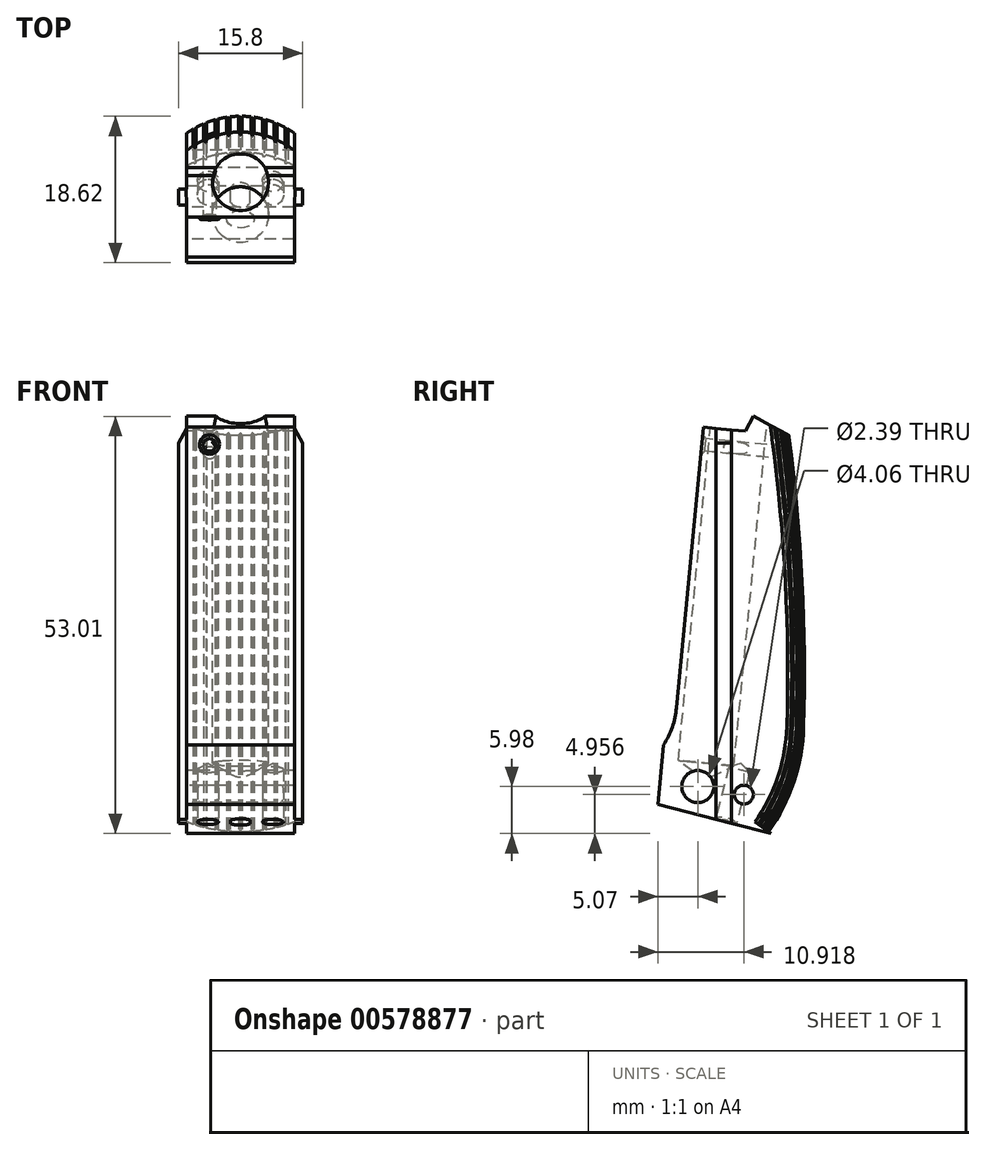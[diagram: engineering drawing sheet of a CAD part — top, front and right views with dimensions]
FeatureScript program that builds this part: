
annotation { "Feature Type Name" : "Feature", "Feature Type Description" : "" }
export const myFeature = defineFeature(function(context is Context, id is Id, definition is map)
    precondition{}
    {
        {
            var Q0;
            Q0=qCreatedBy(makeId("Right.planeOp"),FACE);
            var sketch = newSketch(context, id + "F0", { "sketchPlane" : qUnion([Q0])});
            skCircle(sketch, "E0", {"center": v(0, 0) * mm, "radius": 2.03 * mm});
            skLineSegment(sketch, "E1", {"start": v(-2.71, 10) * mm, "end": v(0.72, 45.66) * mm});
            skLineSegment(sketch, "E2", {"start": v(-5.07, -2.27) * mm, "end": v(-4.34, 5.28) * mm});
            skArc(sketch, "E3", {"start": v(-2.71, 10) * mm, "mid": v(-3.25, 7.55) * mm, "end": v(-4.34, 5.28) * mm});
            skLineSegment(sketch, "E4", {"start": v(-12.8, 17) * mm, "end": v(-15.23, -8.22) * mm, "construction": true});
            skLineSegment(sketch, "E5", {"start": v(0.72, 45.66) * mm, "end": v(6.03, 45.15) * mm});
            skLineSegment(sketch, "E6", {"start": v(-15.2, 11.21) * mm, "end": v(-11.58, 10.86) * mm, "construction": true});
            skLineSegment(sketch, "E7", {"start": v(-5.07, -2.27) * mm, "end": v(9.27, -5.98) * mm});
            skLineSegment(sketch, "E8", {"start": v(6.03, 45.15) * mm, "end": v(7.03, 47.03) * mm});
            skLineSegment(sketch, "E9", {"start": v(7.03, 47.03) * mm, "end": v(11.94, 44.43) * mm});
            skLineSegment(sketch, "E10", {"start": v(0.37, 1.43) * mm, "end": v(-0.87, -3.35) * mm, "construction": true});
            skLineSegment(sketch, "E11", {"start": v(5.64, -1.84) * mm, "end": v(6.05, -0.23) * mm, "construction": true});
            skLineSegment(sketch, "E12", {"start": v(-1.42, 0.37) * mm, "end": v(1.46, -0.38) * mm, "construction": true});
            skLineSegment(sketch, "E13", {"start": v(5.18, -0.85) * mm, "end": v(6.43, -1.18) * mm, "construction": true});
            skPoint(sketch, "E14", {"position": v(5.85, -1.02) * mm});
            skCircle(sketch, "E15", {"center": v(5.85, -1.02) * mm, "radius": 1.2 * mm});
            skLineSegment(sketch, "E16", {"start": v(-2.99, 1.59) * mm, "end": v(23.37, -12.43) * mm, "construction": true});
            skArc(sketch, "E17", {"start": v(13.82, 7.56) * mm, "mid": v(12.55, 0.45) * mm, "end": v(9.27, -5.98) * mm});
            skLineSegment(sketch, "E18", {"start": v(-9.64, 20.45) * mm, "end": v(-11.98, -3.86) * mm, "construction": true});
            skArc(sketch, "E19", {"start": v(10.4, 54.37) * mm, "mid": v(11.22, 49.4) * mm, "end": v(11.94, 44.43) * mm, "construction": true});
            skLineSegment(sketch, "E20", {"start": v(4.58, 39.64) * mm, "end": v(6.07, 55.07) * mm, "construction": true});
            skLineSegment(sketch, "E21", {"start": v(1.76, 47.46) * mm, "end": v(1, 39.47) * mm, "construction": true});
            skLineSegment(sketch, "E22", {"start": v(8.96, 48.04) * mm, "end": v(8.09, 38.96) * mm, "construction": true});
            skPoint(sketch, "E23", {"position": v(8.78, 46.1) * mm});
            skPoint(sketch, "E24", {"position": v(8, -5.64) * mm});
            skLineSegment(sketch, "E25", {"start": v(0, 44.43) * mm, "end": v(17.1, 44.43) * mm, "construction": true});
            skPoint(sketch, "E26", {"position": v(11.94, 44.43) * mm});
            skPoint(sketch, "E27.orphan", {"position": v(10.52, 45.18) * mm});
            skArc(sketch, "E28", {"start": v(10.41, -4.22) * mm, "mid": v(8.76, -6.67) * mm, "end": v(6.82, -8.91) * mm, "construction": true});
            skArc(sketch, "E29", {"start": v(11.94, 44.43) * mm, "mid": v(13.62, 26.03) * mm, "end": v(13.82, 7.56) * mm});
            skPoint(sketch, "E30", {"position": v(-2.83, -2.85) * mm});
            skSolve(sketch);
        }
        {
            var Q0;
            Q0=makeQuery(id+"F0.imprint","IMPRINT",FACE,{"disambiguationData":[TD([[makeQuery(id+"F0.imprint","IMPRINT",EDGE,{"derivedFrom":sQuery(id+"F0.wireOp",EDGE,"E0")}),-1.0]])]});
            extrude(context, id + "F1", {"entities" : qUnion([Q0]), "endBound" : BoundingType.SYMMETRIC, "depth" : 13.67 * mm});
        }
        {
            var Q0;
            Q0=makeQuery(id+"F1.opExtrude","CAP_FACE",FACE,{"disambiguationData":[OSD([sQuery(id+"F0.wireOp",EDGE,"E0"),sQuery(id+"F0.wireOp",EDGE,"E1"),sQuery(id+"F0.wireOp",EDGE,"E2"),sQuery(id+"F0.wireOp",EDGE,"E3"),sQuery(id+"F0.wireOp",EDGE,"E5"),sQuery(id+"F0.wireOp",EDGE,"E7"),sQuery(id+"F0.wireOp",EDGE,"E8"),sQuery(id+"F0.wireOp",EDGE,"E9"),sQuery(id+"F0.wireOp",EDGE,"E15"),sQuery(id+"F0.wireOp",EDGE,"E17"),sQuery(id+"F0.wireOp",EDGE,"E19"),sQuery(id+"F0.wireOp",EDGE,"37774267-7ef6-4adb-93f1-0c025de73d9b")])],"isStart":false});
            var sketch = newSketch(context, id + "F2", { "sketchPlane" : qUnion([Q0])});
            skLineSegment(sketch, "E31", {"start": v(2.29, 45.5) * mm, "end": v(2.29, -4.17) * mm});
            skLineSegment(sketch, "E32", {"start": v(4.27, 45.32) * mm, "end": v(4.27, -4.68) * mm});
            skLineSegment(sketch, "E33.0", {"start": v(2.29, 45.5) * mm, "end": v(4.27, 45.32) * mm});
            skPoint(sketch, "E34.orphan", {"position": v(0.72, 45.66) * mm});
            skPoint(sketch, "E35.orphan", {"position": v(6.03, 45.15) * mm});
            skLineSegment(sketch, "E36.0", {"start": v(2.29, -4.17) * mm, "end": v(4.27, -4.68) * mm});
            skPoint(sketch, "E37.orphan", {"position": v(-5.07, -2.27) * mm});
            skSolve(sketch);
        }
        {
            var Q0;
            Q0=makeQuery(id+"F2.imprint","IMPRINT",FACE,{"disambiguationData":[TD([[makeQuery(id+"F2.imprint","IMPRINT",EDGE,{"derivedFrom":sQuery(id+"F2.wireOp",EDGE,"E31")}),1.0]])]});
            var Q1;
            Q1=qSketchRegion(id+"F2",true);
            extrude(context, id + "F3", {"entities" : qUnion([Q0, Q1]), "operationType" : NewBodyOperationType.ADD, "depth" : 1.07 * mm});
        }
        {
            var Q0;
            {var subQ0=makeQuery(id+"F3.boolean.opBoolean","MERGE",FACE,{"derivedFrom":[makeQuery(id+"F1.opExtrude","SWEPT_FACE",FACE,{"disambiguationData":[OSD([sQuery(id+"F0.wireOp",EDGE,"E5")])]}),makeQuery(id+"F3.opExtrude","SWEPT_FACE",FACE,{"disambiguationData":[OSD([sQuery(id+"F2.wireOp",EDGE,"E33.0")])]})]});Q0=makeQuery(id+"F10.boolean.opBoolean","MERGE",FACE,{"derivedFrom":[subQ0,makeQuery(id+"F10.opPattern","COPY",FACE,{"derivedFrom":subQ0,"instanceName":"1"})]});}
            var sketch = newSketch(context, id + "F4", { "sketchPlane" : qUnion([Q0])});
            skCircle(sketch, "E38", {"center": v(0, 0.76) * mm, "radius": 3.56 * mm});
            skSolve(sketch);
        }
        {
            var Q0;
            Q0=qSketchRegion(id+"F4",true);
            extrude(context, id + "F5", {"entities" : qUnion([Q0]), "operationType" : NewBodyOperationType.REMOVE, "oppositeDirection" : true, "depth" : 42.47 * mm, "hasSecondDirection" : true, "secondDirectionOppositeDirection" : false, "secondDirectionDepth" : 25.4 * mm});
        }
        {
            var Q0;
            Q0=makeQuery(id+"F3.opExtrude","SWEPT_FACE",FACE,{"disambiguationData":[OSD([sQuery(id+"F2.wireOp",EDGE,"E31")])]});
            var sketch = newSketch(context, id + "F6", { "sketchPlane" : qUnion([Q0])});
            skLineSegment(sketch, "E39.0", {"start": v(7.9, 45.5) * mm, "end": v(6.83, 45.5) * mm});
            skLineSegment(sketch, "E40.0", {"start": v(7.9, 45.5) * mm, "end": v(7.9, 43.66) * mm});
            skLineSegment(sketch, "E41", {"start": v(6.83, 45.5) * mm, "end": v(7.9, 43.66) * mm});
            skPoint(sketch, "E42.0.end.orphan", {"position": v(6.83, -4.68) * mm});
            skPoint(sketch, "E43.orphan", {"position": v(7.9, -4.17) * mm});
            skSolve(sketch);
        }
        {
            var Q0;
            Q0=makeQuery(id+"F6.imprint","IMPRINT",FACE,{"disambiguationData":[TD([[makeQuery(id+"F6.imprint","IMPRINT",EDGE,{"derivedFrom":sQuery(id+"F6.wireOp",EDGE,"E39.0")}),1.0]])]});
            extrude(context, id + "F7", {"entities" : qUnion([Q0]), "operationType" : NewBodyOperationType.REMOVE, "endBound" : BoundingType.THROUGH_ALL, "oppositeDirection" : true, "depth" : 25.4 * mm});
        }
        {
            var Q0;
            Q0=qCreatedBy(makeId("Right.planeOp"),FACE);
            var sketch = newSketch(context, id + "F8", { "sketchPlane" : qUnion([Q0])});
            skLineSegment(sketch, "E44.0", {"start": v(-2.49, 3.3) * mm, "end": v(1.05, 2.96) * mm});
            skPoint(sketch, "E45", {"position": v(1.05, 2.96) * mm});
            skLineSegment(sketch, "E46", {"start": v(1.05, 2.96) * mm, "end": v(0.85, 0.83) * mm});
            skLineSegment(sketch, "E47", {"start": v(0.85, 0.83) * mm, "end": v(-2.49, 3.3) * mm});
            skPoint(sketch, "E48.orphan", {"position": v(4.6, 2.62) * mm});
            skSolve(sketch);
        }
        {
            var Q0;
            Q0=qSketchRegion(id+"F8",true);
            var Q1;
            Q1=sQuery(id+"F8.wireOp",EDGE,"E46");
            revolve(context, id + "F9", {"operationType" : NewBodyOperationType.REMOVE, "entities" : qUnion([Q0]), "axis" : qUnion([Q1]), "revolveType" : RevolveType.FULL, "oppositeDirection" : true});
        }
        {
            var Q0;
            Q0=makeQuery(id+"F1.opExtrude","SWEPT_BODY",BODY,{"disambiguationData":[OSD([sQuery(id+"F0.wireOp",EDGE,"E0"),sQuery(id+"F0.wireOp",EDGE,"E1"),sQuery(id+"F0.wireOp",EDGE,"E2"),sQuery(id+"F0.wireOp",EDGE,"E3"),sQuery(id+"F0.wireOp",EDGE,"E5"),sQuery(id+"F0.wireOp",EDGE,"E7"),sQuery(id+"F0.wireOp",EDGE,"E8"),sQuery(id+"F0.wireOp",EDGE,"E9"),sQuery(id+"F0.wireOp",EDGE,"E15"),sQuery(id+"F0.wireOp",EDGE,"E17"),sQuery(id+"F0.wireOp",EDGE,"E19"),sQuery(id+"F0.wireOp",EDGE,"37774267-7ef6-4adb-93f1-0c025de73d9b")])]});
            var Q1;
            Q1=qCreatedBy(makeId("Right.planeOp"),FACE);
            mirror(context, id + "F10", {"operationType" : NewBodyOperationType.ADD, "entities" : qUnion([Q0]), "mirrorPlane" : qUnion([Q1])});
        }
        {
            var Q0;
            {var subQ0=makeQuery(id+"F3.boolean.opBoolean","MERGE",FACE,{"derivedFrom":[makeQuery(id+"F1.opExtrude","SWEPT_FACE",FACE,{"disambiguationData":[OSD([sQuery(id+"F0.wireOp",EDGE,"E7")])]}),makeQuery(id+"F3.opExtrude","SWEPT_FACE",FACE,{"disambiguationData":[OSD([sQuery(id+"F2.wireOp",EDGE,"E36.0")])]})]});Q0=makeQuery(id+"F10.boolean.opBoolean","MERGE",FACE,{"derivedFrom":[subQ0,makeQuery(id+"F10.opPattern","COPY",FACE,{"derivedFrom":subQ0,"instanceName":"1"})]});}
            var sketch = newSketch(context, id + "F11", { "sketchPlane" : qUnion([Q0])});
            skLineSegment(sketch, "E49", {"start": v(-7.83, 0) * mm, "end": v(8.84, 0) * mm, "construction": true});
            skLineSegment(sketch, "E50", {"start": v(4.13, -4.57) * mm, "end": v(-4.13, -4.57) * mm, "construction": true});
            skLineSegment(sketch, "E51", {"start": v(0, 3.9) * mm, "end": v(0, -12.72) * mm, "construction": true});
            skCircle(sketch, "E52", {"center": v(-4.13, -4.57) * mm, "radius": 1.35 * mm});
            skCircle(sketch, "E53", {"center": v(4.13, -4.57) * mm, "radius": 1.35 * mm});
            skPoint(sketch, "E54", {"position": v(0, -4.57) * mm});
            skSolve(sketch);
        }
        {
            var Q0;
            Q0=sQuery(id+"F11.wireOp",VERTEX,"E52.center");
            var Q1;
            Q1=sQuery(id+"F11.wireOp",VERTEX,"E50.start");
            var Q2;
            Q2=makeQuery(id+"F1.opExtrude","SWEPT_BODY",BODY,{"disambiguationData":[OSD([sQuery(id+"F0.wireOp",EDGE,"E0"),sQuery(id+"F0.wireOp",EDGE,"E1"),sQuery(id+"F0.wireOp",EDGE,"E2"),sQuery(id+"F0.wireOp",EDGE,"E3"),sQuery(id+"F0.wireOp",EDGE,"E5"),sQuery(id+"F0.wireOp",EDGE,"E7"),sQuery(id+"F0.wireOp",EDGE,"E8"),sQuery(id+"F0.wireOp",EDGE,"E9"),sQuery(id+"F0.wireOp",EDGE,"E15"),sQuery(id+"F0.wireOp",EDGE,"E17"),sQuery(id+"F0.wireOp",EDGE,"E19"),sQuery(id+"F0.wireOp",EDGE,"37774267-7ef6-4adb-93f1-0c025de73d9b")])]});
            hole(context, id + "F12", {"style" : HoleStyle.SIMPLE, "holeDiameter" : 2.7 * mm, "endStyle" : HoleEndStyle.BLIND, "holeDepth" : 6.86 * mm, "locations" : qUnion([Q0, Q1]), "scope" : qUnion([Q2])});
        }
        {
            var Q0;
            Q0=sQuery(id+"F11.wireOp",EDGE,"E50");
            cPlane(context, id + "F13", {"entities" : qUnion([Q0]), "cplaneType" : CPlaneType.LINE_ANGLE, "offset" : 152.4 * mm, "angle" : 14.5 * degree, "width" : 152.4 * mm, "height" : 152.4 * mm});
        }
        {
            var Q0;
            Q0=qCreatedBy(id+"F13.planeOp",FACE);
            var sketch = newSketch(context, id + "F14", { "sketchPlane" : qUnion([Q0])});
            skPoint(sketch, "E55.0", {"position": v(0, -3.46) * mm});
            skArc(sketch, "E56", {"start": v(1.6, -3.46) * mm, "mid": v(0, -2.96) * mm, "end": v(-1.6, -3.46) * mm});
            skLineSegment(sketch, "E57", {"start": v(0, -3.46) * mm, "end": v(0, -7.65) * mm, "construction": true});
            skLineSegment(sketch, "E58.0", {"start": v(4.13, -3.46) * mm, "end": v(-4.13, -3.46) * mm, "construction": true});
            skLineSegment(sketch, "E59", {"start": v(1.6, -3.46) * mm, "end": v(-1.6, -3.46) * mm});
            skLineSegment(sketch, "E60", {"start": v(1.48, -5.72) * mm, "end": v(-1.75, -5.72) * mm, "construction": true});
            skSolve(sketch);
        }
        {
            var Q0;
            Q0=qSketchRegion(id+"F14",true);
            var Q1;
            Q1=sQuery(id+"F14.wireOp",EDGE,"E60");
            revolve(context, id + "F15", {"operationType" : NewBodyOperationType.REMOVE, "entities" : qUnion([Q0]), "axis" : qUnion([Q1]), "revolveType" : RevolveType.FULL, "oppositeDirection" : true});
        }
        {
            var Q0;
            Q0=makeQuery(id+"F11.imprint","IMPRINT",FACE,{"disambiguationData":[TD([[makeQuery(id+"F11.imprint","IMPRINT",EDGE,{"derivedFrom":sQuery(id+"F11.wireOp",EDGE,"E52")}),-1.0]])]});
            var sketch = newSketch(context, id + "F16", { "sketchPlane" : qUnion([Q0])});
            skLineSegment(sketch, "E61", {"start": v(1.24, -2.45) * mm, "end": v(1.24, -6.25) * mm});
            skLineSegment(sketch, "E62", {"start": v(1.24, -6.25) * mm, "end": v(2.03, -6.25) * mm});
            skLineSegment(sketch, "E63", {"start": v(2.03, -6.25) * mm, "end": v(2.03, -2.5) * mm});
            skLineSegment(sketch, "E64", {"start": v(2.03, -2.5) * mm, "end": v(1.24, -2.45) * mm});
            skLineSegment(sketch, "E65", {"start": v(-1.24, -2.45) * mm, "end": v(-1.24, -6.43) * mm});
            skLineSegment(sketch, "E66", {"start": v(-1.24, -6.43) * mm, "end": v(-2.17, -6.43) * mm});
            skLineSegment(sketch, "E67", {"start": v(-2.17, -6.43) * mm, "end": v(-2.17, -2.44) * mm});
            skLineSegment(sketch, "E68", {"start": v(-2.17, -2.44) * mm, "end": v(-1.24, -2.45) * mm});
            skSolve(sketch);
        }
        {
            var Q0;
            Q0=qSketchRegion(id+"F16",true);
            extrude(context, id + "F17", {"entities" : qUnion([Q0]), "operationType" : NewBodyOperationType.ADD, "oppositeDirection" : true, "depth" : 0.5 * mm});
        }
        {
            var Q0;
            Q0=qCreatedBy(makeId("Right.planeOp"),FACE);
            var sketch = newSketch(context, id + "F18", { "sketchPlane" : qUnion([Q0])});
            skArc(sketch, "E69.0", {"start": v(11.94, 44.43) * mm, "mid": v(13.62, 26.03) * mm, "end": v(13.82, 7.56) * mm});
            skArc(sketch, "E70.0", {"start": v(11.49, 47.66) * mm, "mid": v(11.72, 46.04) * mm, "end": v(11.94, 44.43) * mm});
            skArc(sketch, "E71.0", {"start": v(13.82, 7.56) * mm, "mid": v(12.55, 0.45) * mm, "end": v(9.27, -5.98) * mm});
            skArc(sketch, "E72.0", {"start": v(10.41, -4.22) * mm, "mid": v(8.76, -6.67) * mm, "end": v(6.82, -8.91) * mm});
            skPoint(sketch, "E73.0", {"position": v(7.03, 47.03) * mm});
            skLineSegment(sketch, "E74", {"start": v(7.03, 47.03) * mm, "end": v(14.3, 48.05) * mm, "construction": true});
            skPoint(sketch, "E75.orphan", {"position": v(10.4, 54.37) * mm});
            skSolve(sketch);
        }
        {
            var Q0;
            {var subQ0=sQuery(id+"F0.wireOp",EDGE,"E8");var subQ1=sQuery(id+"F0.wireOp",EDGE,"E9");Q0=makeQuery(id+"F5.boolean.opBoolean","SPLIT",EDGE,{"disambiguationData":[TD([makeQuery(id+"F1.opExtrude","CAP_FACE",FACE,{"disambiguationData":[OSD([sQuery(id+"F0.wireOp",EDGE,"E0"),sQuery(id+"F0.wireOp",EDGE,"E1"),sQuery(id+"F0.wireOp",EDGE,"E2"),sQuery(id+"F0.wireOp",EDGE,"E3"),sQuery(id+"F0.wireOp",EDGE,"E5"),sQuery(id+"F0.wireOp",EDGE,"E7"),subQ0,subQ1,sQuery(id+"F0.wireOp",EDGE,"E15"),sQuery(id+"F0.wireOp",EDGE,"E17"),sQuery(id+"F0.wireOp",EDGE,"37774267-7ef6-4adb-93f1-0c025de73d9b"),sQuery(id+"F0.wireOp",EDGE,"E29")])],"isStart":false})])],"derivedFrom":makeQuery(id+"F1.opExtrude","SWEPT_EDGE",EDGE,{"disambiguationData":[OSD([subQ0,subQ1])]})});}
            cPlane(context, id + "F19", {"entities" : qUnion([Q0]), "cplaneType" : CPlaneType.LINE_ANGLE, "offset" : 152.4 * mm, "angle" : 82 * degree, "width" : 152.4 * mm, "height" : 152.4 * mm});
        }
        {
            var Q0;
            Q0=qCreatedBy(id+"F19.planeOp",FACE);
            var sketch = newSketch(context, id + "F20", { "sketchPlane" : qUnion([Q0])});
            skLineSegment(sketch, "E76", {"start": v(0, 0) * mm, "end": v(0, -1.4) * mm, "construction": true});
            skLineSegment(sketch, "E77", {"start": v(0, 0) * mm, "end": v(-1.15, 13.1) * mm, "construction": true});
            skLineSegment(sketch, "E78", {"start": v(0, 0) * mm, "end": v(-2.29, 12.96) * mm, "construction": true});
            skLineSegment(sketch, "E79", {"start": v(0, 0) * mm, "end": v(-3.39, 12.64) * mm, "construction": true});
            skLineSegment(sketch, "E80", {"start": v(0, 0) * mm, "end": v(-4.56, 12.52) * mm, "construction": true});
            skLineSegment(sketch, "E81", {"start": v(-7.62, 14.9) * mm, "end": v(-7.62, 21.38) * mm});
            skLineSegment(sketch, "E82", {"start": v(0, 0) * mm, "end": v(1.19, 13.57) * mm, "construction": true});
            skLineSegment(sketch, "E83", {"start": v(0, 0) * mm, "end": v(2.36, 13.39) * mm, "construction": true});
            skLineSegment(sketch, "E84", {"start": v(0, 0) * mm, "end": v(3.6, 13.4) * mm, "construction": true});
            skLineSegment(sketch, "E85", {"start": v(0, 0) * mm, "end": v(4.71, 12.95) * mm, "construction": true});
            skLineSegment(sketch, "E86", {"start": v(7.56, 14.95) * mm, "end": v(7.4, 22.87) * mm});
            skLineSegment(sketch, "E87", {"start": v(7.4, 22.87) * mm, "end": v(-7.62, 21.38) * mm});
            skLineSegment(sketch, "E88.0", {"start": v(0, 18) * mm, "end": v(0, 18) * mm});
            skPoint(sketch, "E89", {"position": v(0, 17.64) * mm});
            skArc(sketch, "E90", {"start": v(-9.48, 12.97) * mm, "mid": v(0.07, 17.64) * mm, "end": v(9.56, 12.86) * mm});
            skArc(sketch, "E91", {"start": v(-11.9, 6.25) * mm, "mid": v(0, 17.26) * mm, "end": v(11.9, 6.26) * mm, "construction": true});
            skLineSegment(sketch, "E92", {"start": v(6.02, 16.02) * mm, "end": v(5.75, 15.79) * mm});
            skLineSegment(sketch, "E93", {"start": v(4.67, 16.7) * mm, "end": v(4.4, 16.42) * mm});
            skLineSegment(sketch, "E94", {"start": v(4.4, 16.42) * mm, "end": v(4.29, 16.85) * mm});
            skLineSegment(sketch, "E95", {"start": v(3.24, 17.2) * mm, "end": v(2.98, 16.89) * mm});
            skLineSegment(sketch, "E96", {"start": v(2.98, 16.89) * mm, "end": v(2.82, 17.3) * mm});
            skLineSegment(sketch, "E97", {"start": v(1.75, 17.52) * mm, "end": v(1.5, 17.17) * mm});
            skLineSegment(sketch, "E98", {"start": v(1.5, 17.17) * mm, "end": v(1.31, 17.57) * mm});
            skLineSegment(sketch, "E99", {"start": v(0.22, 17.64) * mm, "end": v(0, 17.26) * mm});
            skLineSegment(sketch, "E100", {"start": v(0, 17.26) * mm, "end": v(-0.22, 17.64) * mm});
            skLineSegment(sketch, "E101", {"start": v(-1.31, 17.57) * mm, "end": v(-1.5, 17.17) * mm});
            skLineSegment(sketch, "E102", {"start": v(-1.5, 17.17) * mm, "end": v(-1.75, 17.52) * mm});
            skLineSegment(sketch, "E103", {"start": v(-2.82, 17.3) * mm, "end": v(-2.98, 16.89) * mm});
            skLineSegment(sketch, "E104", {"start": v(-2.98, 16.89) * mm, "end": v(-3.24, 17.2) * mm});
            skLineSegment(sketch, "E105", {"start": v(-4.29, 16.85) * mm, "end": v(-4.4, 16.42) * mm});
            skLineSegment(sketch, "E106", {"start": v(-4.4, 16.42) * mm, "end": v(-4.67, 16.7) * mm});
            skLineSegment(sketch, "E107", {"start": v(-5.67, 16.2) * mm, "end": v(-5.75, 15.79) * mm});
            skLineSegment(sketch, "E108", {"start": v(-5.75, 15.79) * mm, "end": v(-6.02, 16.02) * mm});
            skLineSegment(sketch, "E109", {"start": v(-6.02, 16.02) * mm, "end": v(-5.97, 15.98) * mm});
            skLineSegment(sketch, "E110", {"start": v(5.75, 15.79) * mm, "end": v(5.67, 16.2) * mm});
            skSolve(sketch);
        }
        {
            var Q0;
            Q0=qSketchRegion(id+"F20",true);
            var Q1;
            Q1=sQuery(id+"F18.wireOp",EDGE,"E69.0");
            var Q2;
            Q2=sQuery(id+"F18.wireOp",EDGE,"E70.0");
            var Q3;
            Q3=sQuery(id+"F18.wireOp",EDGE,"E71.0");
            sweep(context, id + "F21", {"operationType" : NewBodyOperationType.REMOVE, "profiles" : qUnion([Q0]), "path" : qUnion([Q1, Q2, Q3])});
        }
        {
            var Q0;
            Q0=makeQuery(id+"F1.opExtrude","SWEPT_FACE",FACE,{"disambiguationData":[OSD([sQuery(id+"F0.wireOp",EDGE,"E1")])]});
            var sketch = newSketch(context, id + "F22", { "sketchPlane" : qUnion([Q0])});
            skPoint(sketch, "E111", {"position": v(-3.94, 43.28) * mm});
            skSolve(sketch);
        }
        {
            var Q0;
            Q0=sQuery(id+"F22.wireOp",VERTEX,"E111");
            var Q1;
            Q1=makeQuery(id+"F1.opExtrude","SWEPT_BODY",BODY,{"disambiguationData":[OSD([sQuery(id+"F0.wireOp",EDGE,"E0"),sQuery(id+"F0.wireOp",EDGE,"E1"),sQuery(id+"F0.wireOp",EDGE,"E2"),sQuery(id+"F0.wireOp",EDGE,"E3"),sQuery(id+"F0.wireOp",EDGE,"E5"),sQuery(id+"F0.wireOp",EDGE,"E7"),sQuery(id+"F0.wireOp",EDGE,"E8"),sQuery(id+"F0.wireOp",EDGE,"E9"),sQuery(id+"F0.wireOp",EDGE,"E15"),sQuery(id+"F0.wireOp",EDGE,"E17"),sQuery(id+"F0.wireOp",EDGE,"37774267-7ef6-4adb-93f1-0c025de73d9b"),sQuery(id+"F0.wireOp",EDGE,"E29")])]});
            hole(context, id + "F23", {"style" : HoleStyle.C_SINK, "holeDiameter" : 1.6 * mm, "cSinkDiameter" : 2.5 * mm, "endStyle" : HoleEndStyle.THROUGH, "locations" : qUnion([Q0]), "scope" : qUnion([Q1]), "cSinkAngle" : 90 * degree});
        }
    });
